# Revit family: Montageschiene 27- 18-1,25  2m, V2A
name_source: partatom
category: HLS-Bauteile
revit_build: Autodesk Revit 2017 (Build: 20190507_1515(x64)
units: mm (PartAtom-declared; Revit-internal decimal feet)

## family parameters
Arbeitsebenenbasiert = Ja
Beim Laden mit Abzugskörper schneiden = Nein
Bemaßung runder Anschluss = Durchmesser verwenden
Gemeinsam genutzt = Ja
Immer vertikal = Nein
Raumberechnungspunkt = Nein
Teiletyp = Normal

## types (1)
- C-Profil  27- 18-1,25  L=2000, V2A
    Abmessung = 27/18/1.25 mm
    Artikelnummer = 0800050
    Breite = 27 mm  [stored 0.0885827 ft]
    Bund = 800 m
    EAN = 4250928419170
    Fabrikat = MEFA
    Firma = MEFA Befestigungs- und Montagesysteme GmbH
    Fläche (schwächster Profilquerschnitt) = 0 m²
    Gewicht = 0,61 kg
    Höhe = 18 mm
    Kurztext1 = Montageschiene C-Profil V2A
    Kurztext2 = 27 / 18 / 1,25 mm L= 2 m
    Langloch = 10.5 x 38.5 mm
    Länge = 2000 mm  [stored 6.56168 ft]
    Material = Edelstahl
    Mengeneinheit = m
    Schlitzbreite = 14 mm
    Schwerpunktabstand eo = 0,85 cm
    Schwerpunktabstand eu = 0,95 cm
    Schwerpunktabstand ez = 1,35 cm
    Streckgrenze = 230 N/mm²
    Stärke = 1 mm  [stored 0.00328084 ft]
    Torsionswiderstandsmoment Wt = cm³
    Trägheitsradius iy = 0,66 cm
    Trägheitsradius iz = 1,15 cm
    Vorgabe-Ansicht = 1219 mm
    Widerstandsmoment Wy = 0,31 cm³
    Widerstandsmoment Wz = 0,66 cm³
    vpe = 20 m

note: [stored X ft] marks values corroborated as IEEE doubles in the binary element streams (Revit-internal decimal feet)
